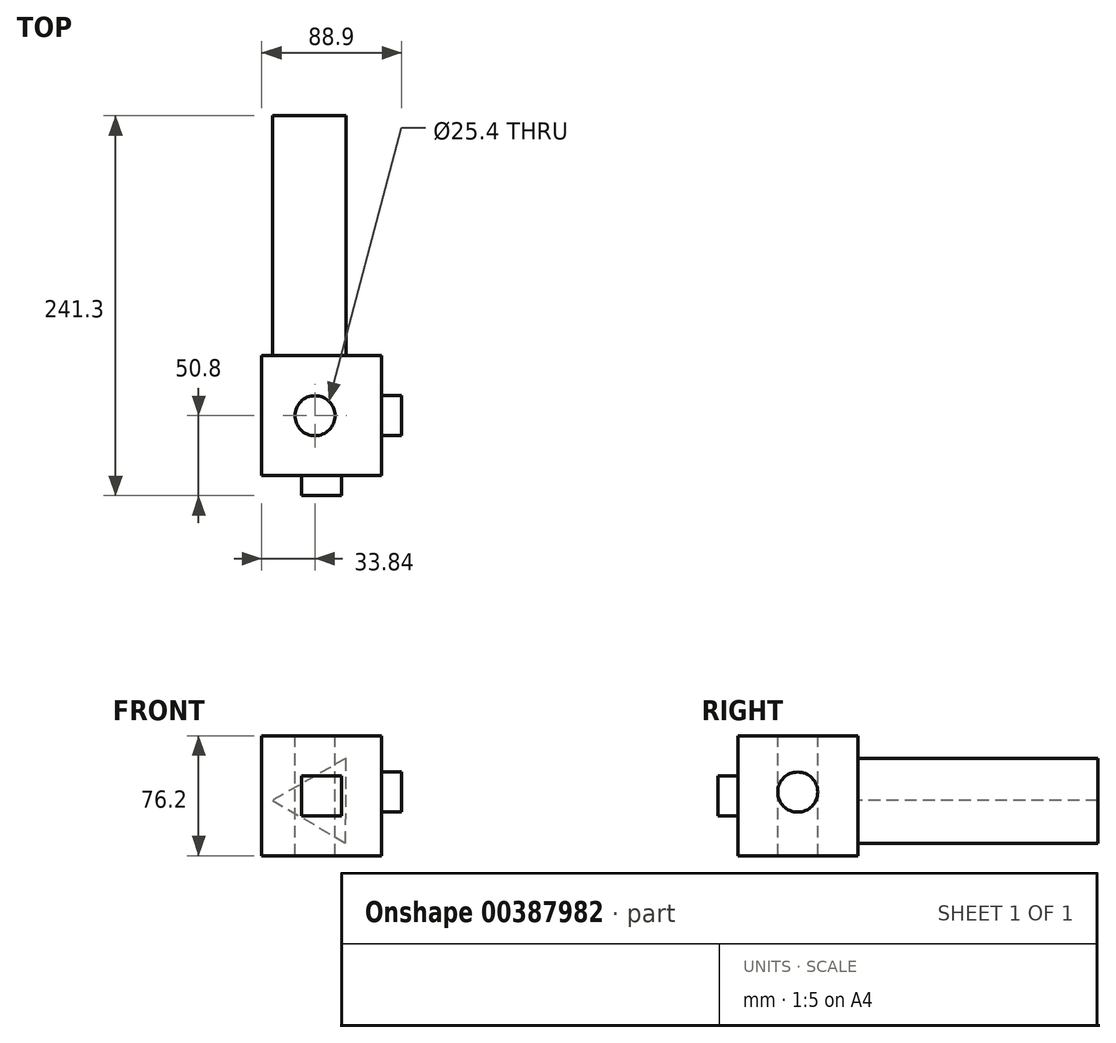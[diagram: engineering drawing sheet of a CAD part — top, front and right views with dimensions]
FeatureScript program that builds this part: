
annotation { "Feature Type Name" : "Feature", "Feature Type Description" : "" }
export const myFeature = defineFeature(function(context is Context, id is Id, definition is map)
    precondition{}
    {
        {
            var Q0;
            Q0=qCreatedBy(makeId("Front.planeOp"),FACE);
            var sketch = newSketch(context, id + "F0", { "sketchPlane" : qUnion([Q0])});
            skLineSegment(sketch, "E0.bottom", {"start": v(-33.84, -40.42) * mm, "end": v(42.36, -40.42) * mm});
            skLineSegment(sketch, "E0.top", {"start": v(-33.84, 35.78) * mm, "end": v(42.36, 35.78) * mm});
            skLineSegment(sketch, "E0.left", {"start": v(-33.84, -40.42) * mm, "end": v(-33.84, 35.78) * mm});
            skLineSegment(sketch, "E0.right", {"start": v(42.36, -40.42) * mm, "end": v(42.36, 35.78) * mm});
            skSolve(sketch);
        }
        {
            var Q0;
            Q0=makeQuery(id+"F0.imprint","IMPRINT",FACE,{"disambiguationData":[TD([[makeQuery(id+"F0.imprint","IMPRINT",EDGE,{"derivedFrom":sQuery(id+"F0.wireOp",EDGE,"E0.bottom")}),1.0]])]});
            extrude(context, id + "F1", {"entities" : qUnion([Q0]), "depth" : 76.2 * mm});
        }
        {
            var Q0;
            Q0=makeQuery(id+"F1.opExtrude","SWEPT_FACE",FACE,{"disambiguationData":[OSD([sQuery(id+"F0.wireOp",EDGE,"E0.top")])]});
            var sketch = newSketch(context, id + "F2", { "sketchPlane" : qUnion([Q0])});
            skPoint(sketch, "E1", {"position": v(0, -38.1) * mm});
            skSolve(sketch);
        }
        {
            var Q0;
            Q0=sQuery(id+"F2.wireOp",VERTEX,"E1");
            var Q1;
            Q1=makeQuery(id+"F1.opExtrude","SWEPT_BODY",BODY,{"disambiguationData":[OSD([sQuery(id+"F0.wireOp",EDGE,"E0.bottom"),sQuery(id+"F0.wireOp",EDGE,"E0.top"),sQuery(id+"F0.wireOp",EDGE,"E0.left"),sQuery(id+"F0.wireOp",EDGE,"E0.right")])]});
            hole(context, id + "F3", {"style" : HoleStyle.SIMPLE, "endStyle" : HoleEndStyle.THROUGH, "holeDiameter" : 25.4 * mm, "isTappedThrough" : true, "tappedDepth" : 12.7 * mm, "tapClearance" : 3, "locations" : qUnion([Q0]), "scope" : qUnion([Q1])});
        }
        {
            var Q0;
            Q0=makeQuery(id+"F1.opExtrude","CAP_FACE",FACE,{"disambiguationData":[OSD([sQuery(id+"F0.wireOp",EDGE,"E0.bottom"),sQuery(id+"F0.wireOp",EDGE,"E0.top"),sQuery(id+"F0.wireOp",EDGE,"E0.left"),sQuery(id+"F0.wireOp",EDGE,"E0.right")])],"isStart":false});
            var sketch = newSketch(context, id + "F4", { "sketchPlane" : qUnion([Q0])});
            skLineSegment(sketch, "E2.bottom", {"start": v(-8.44, -15.02) * mm, "end": v(16.96, -15.02) * mm});
            skLineSegment(sketch, "E2.top", {"start": v(-8.44, 10.38) * mm, "end": v(16.96, 10.38) * mm});
            skLineSegment(sketch, "E2.left", {"start": v(-8.44, -15.02) * mm, "end": v(-8.44, 10.38) * mm});
            skLineSegment(sketch, "E2.right", {"start": v(16.96, -15.02) * mm, "end": v(16.96, 10.38) * mm});
            skSolve(sketch);
        }
        {
            var Q0;
            Q0=makeQuery(id+"F4.imprint","IMPRINT",FACE,{"disambiguationData":[TD([[makeQuery(id+"F4.imprint","IMPRINT",EDGE,{"derivedFrom":sQuery(id+"F4.wireOp",EDGE,"E2.bottom")}),1.0]])]});
            extrude(context, id + "F5", {"entities" : qUnion([Q0]), "operationType" : NewBodyOperationType.ADD, "depth" : 12.7 * mm});
        }
        {
            var Q0;
            Q0=makeQuery(id+"F1.opExtrude","SWEPT_FACE",FACE,{"disambiguationData":[OSD([sQuery(id+"F0.wireOp",EDGE,"E0.right")])]});
            var sketch = newSketch(context, id + "F6", { "sketchPlane" : qUnion([Q0])});
            skCircle(sketch, "E3", {"center": v(-38.1, 0) * mm, "radius": 12.7 * mm});
            skSolve(sketch);
        }
        {
            var Q0;
            Q0=makeQuery(id+"F6.imprint","IMPRINT",FACE,{"disambiguationData":[TD([[makeQuery(id+"F6.imprint","IMPRINT",EDGE,{"derivedFrom":sQuery(id+"F6.wireOp",EDGE,"E3")}),1.0]])]});
            extrude(context, id + "F7", {"entities" : qUnion([Q0]), "operationType" : NewBodyOperationType.ADD, "depth" : 12.7 * mm});
        }
        {
            var Q0;
            Q0=makeQuery(id+"F1.opExtrude","CAP_FACE",FACE,{"disambiguationData":[OSD([sQuery(id+"F0.wireOp",EDGE,"E0.bottom"),sQuery(id+"F0.wireOp",EDGE,"E0.top"),sQuery(id+"F0.wireOp",EDGE,"E0.left"),sQuery(id+"F0.wireOp",EDGE,"E0.right")])],"isStart":true});
            var sketch = newSketch(context, id + "F8", { "sketchPlane" : qUnion([Q0])});
            skPoint(sketch, "E4", {"position": v(-2.09, -1.69) * mm});
            skCircle(sketch, "E5.cCircle", {"center": v(-4.05, -5.4) * mm, "radius": 15.57 * mm, "construction": true});
            skLineSegment(sketch, "E5.0", {"start": v(-19.72, 21.5) * mm, "end": v(27.1, -5.3) * mm});
            skLineSegment(sketch, "E5.1", {"start": v(27.1, -5.3) * mm, "end": v(-19.52, -32.44) * mm});
            skLineSegment(sketch, "E5.2", {"start": v(-19.52, -32.44) * mm, "end": v(-19.72, 21.5) * mm});
            skPoint(sketch, "E5.0.midPoint", {"position": v(3.7, 8.1) * mm});
            skSolve(sketch);
        }
        {
            var Q0;
            Q0=makeQuery(id+"F8.imprint","IMPRINT",FACE,{"disambiguationData":[TD([[makeQuery(id+"F8.imprint","IMPRINT",EDGE,{"derivedFrom":sQuery(id+"F8.wireOp",EDGE,"E5.0")}),-1.0]])]});
            extrude(context, id + "F9", {"entities" : qUnion([Q0]), "operationType" : NewBodyOperationType.ADD, "depth" : 152.4 * mm});
        }
    });
